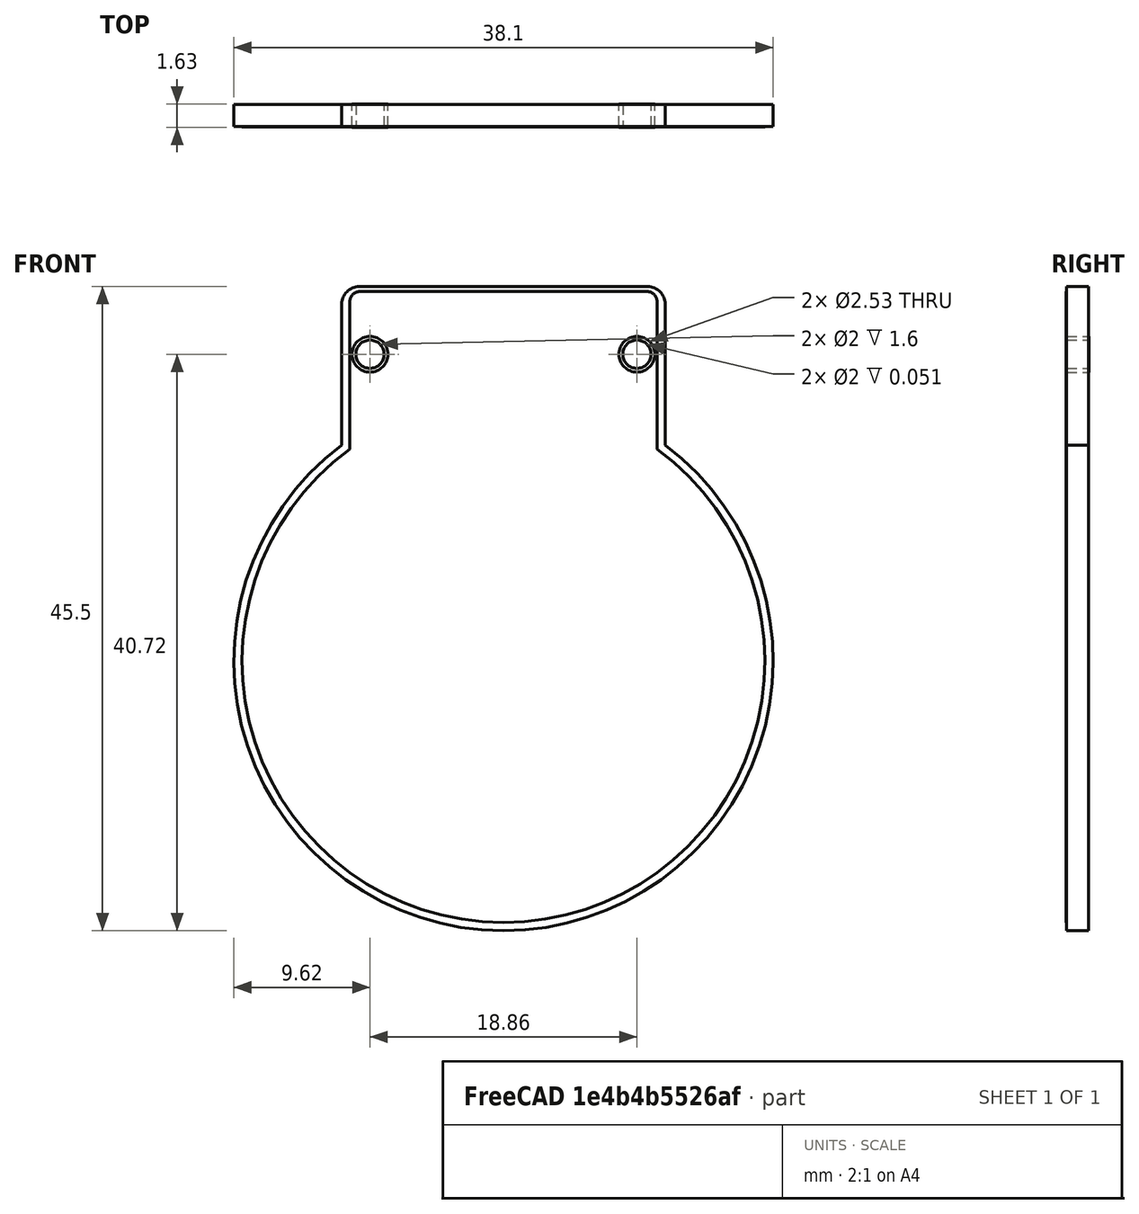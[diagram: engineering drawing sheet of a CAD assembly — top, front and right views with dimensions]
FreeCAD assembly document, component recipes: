
FREECAD ASSEMBLY — COMPONENT RECIPES ("gc9a01")

This assembly document has 2 components, labeled P0..P1 below (a component is one placed body or linked part). 0 of them carry a construction recipe — the FreeCAD feature program that regenerates the part from scratch, quoted from this document or its linked companion documents; the rest are supplied as boundary geometry only. No exploded tour is included for this assembly.
COMPONENT P0 — geometry summary ("TFT-Round-1.28 v1"; no construction recipe available for this part):
  bounding box: 38.6 x 35.6 x 1.6 mm
  tessellated surface: 2,956 triangles
  volume: 1675 mm^3 (75% of its bounding box)
  symmetry: 2-fold rotationally symmetric about the z axis; mirror-symmetric across its x mid-plane
COMPONENT P1 — geometry summary ("Component6"; no construction recipe available for this part):
  bounding box: 17.0 x 1.8 x 1.2 mm
  tessellated surface: 20,896 triangles
  volume: 4 mm^3 (12% of its bounding box)
  symmetry: 2-fold rotationally symmetric about the y axis; mirror-symmetric across its x mid-plane, z mid-plane
PROVENANCE & LICENSES
A FreeCAD (.FCStd) document from a public repository crawl; recipes are the document's own serialized feature recipes (and, for linked parts, companion documents' recipes).
License: cc0-1.0.
